FCSTD DOCUMENT  (FreeCAD 0.20R29410 (Git))
Label: StarTrekInsigniaExtrusion
License: All rights reserved
LicenseURL: http://en.wikipedia.org/wiki/All_rights_reserved
objects: Sketcher::SketchObject×2, Image::ImagePlane×1, Part::Part2DObjectPython×1, PartDesign::Body×1
note: 4 computed .brp shape members not serialized (recipe doc carries the construction recipe); baked Part::Feature solids carry a one-line shape summary decoded from their .brp

FEATURE [Image::ImagePlane] ImagePlane
  Placement = pos=(-0.5,-5,0) rot=(0,0,1;0rad)
  XSize = 37.5907
  YSize = 60.1187
FEATURE [Sketcher::SketchObject] Sketch
  FullyConstrained = true
  MapMode = 5
  Support = -> [XY_Plane]
  sketch-geometry (74):
    g0-g3: Circle x4 (B-spline internal-alignment scaffolding for g4; pole/knot coordinates omitted)
    g4: BSplineCurve PolesCount=4 KnotsCount=2 Degree=3 IsPeriodic=0
    g5: GeomPoint X=-18.4513 Y=-34.513 Z=0
    g6: GeomPoint X=-0.733176 Y=25.0097 Z=0
    g7-g10: Circle x4 (B-spline internal-alignment scaffolding for g11; pole/knot coordinates omitted)
    g11: BSplineCurve PolesCount=4 KnotsCount=2 Degree=3 IsPeriodic=0
    g12: GeomPoint X=-0.733176 Y=25.0097 Z=0
    g13: GeomPoint X=17.9425 Y=-29.3614 Z=0
    g14-g22: Circle x9 (B-spline internal-alignment scaffolding for g23; pole/knot coordinates omitted)
    g23: BSplineCurve PolesCount=9 KnotsCount=7 Degree=3 IsPeriodic=0
    g24-g30: GeomPoint x7 (B-spline internal-alignment scaffolding for g23; pole/knot coordinates omitted)
    g31-g34: Circle x4 (B-spline internal-alignment scaffolding for g35; pole/knot coordinates omitted)
    g35: BSplineCurve PolesCount=4 KnotsCount=2 Degree=3 IsPeriodic=0
    g36: GeomPoint X=-16.2191 Y=-26.8064 Z=0
    g37: GeomPoint X=-0.795845 Y=21.9646 Z=0
    g38-g41: Circle x4 (B-spline internal-alignment scaffolding for g42; pole/knot coordinates omitted)
    g42: BSplineCurve PolesCount=4 KnotsCount=2 Degree=3 IsPeriodic=0
    g43: GeomPoint X=-0.795845 Y=21.9646 Z=0
    g44: GeomPoint X=14.3586 Y=-17.0278 Z=0
    g45-g54: Circle x10 (B-spline internal-alignment scaffolding for g55; pole/knot coordinates omitted)
    g55: BSplineCurve PolesCount=10 KnotsCount=8 Degree=3 IsPeriodic=0
    g56-g63: GeomPoint x8 (B-spline internal-alignment scaffolding for g55; pole/knot coordinates omitted)
    g64: LineSegment StartX=0 StartY=17.9558 StartZ=0 EndX=-1.83675 EndY=1.71768 EndZ=0
    g65: LineSegment StartX=-1.83675 StartY=1.71768 StartZ=0 EndX=-5.87472 EndY=0.00675 EndZ=0
    g66: LineSegment StartX=-5.87472 StartY=0.00675 StartZ=0 EndX=-2.54091 EndY=-1.79051 EndZ=0
    g67: LineSegment StartX=-2.54091 StartY=-1.79051 StartZ=0 EndX=-3.15906 EndY=-7.34318 EndZ=0
    g68: LineSegment StartX=-3.15906 StartY=-7.34318 StartZ=0 EndX=4e-16 EndY=-2.82733 EndZ=0
    g69: LineSegment StartX=4e-16 StartY=-2.82733 StartZ=0 EndX=3.15906 EndY=-7.34318 EndZ=0
    g70: LineSegment StartX=3.15906 StartY=-7.34318 StartZ=0 EndX=2.54091 EndY=-1.79051 EndZ=0
    g71: LineSegment StartX=2.54091 StartY=-1.79051 StartZ=0 EndX=5.87472 EndY=0.00675 EndZ=0
    g72: LineSegment StartX=5.87472 StartY=0.00675 StartZ=0 EndX=1.83675 EndY=1.71768 EndZ=0
    g73: LineSegment StartX=1.83675 StartY=1.71768 StartZ=0 EndX=0 EndY=17.9558 EndZ=0
  constraints (74):
    c: Weight(g0) = 1
    c: Equal(g0,g1)
    c: Equal(g0,g2)
    c: Equal(g0,g3)
    c: InternalAlignment(g0-g3 -> g4) x4
    c: InternalAlignment(g5,g4)
    c: InternalAlignment(g6,g4)
    c: Weight(g7) = 1
    c: Coincident(g11,g4)
    c: Equal(g7,g8)
    c: Equal(g7,g9)
    c: Equal(g7,g10)
    c: InternalAlignment(g7-g10 -> g11) x4
    c: InternalAlignment(g12,g11)
    c: InternalAlignment(g13,g11)
    c: Weight(g14) = 1
    c: Coincident(g23,g4)
    c: Equal(g14, g15-g22) x8
    c: Coincident(g23,g11)
    c: InternalAlignment(g14-g22 -> g23) x9
    c: InternalAlignment(g24-g30 -> g23) x7
    c: Weight(g31) = 1
    c: Equal(g31,g32)
    c: Equal(g31,g33)
    c: Equal(g31,g34)
    c: InternalAlignment(g31-g34 -> g35) x4
    c: InternalAlignment(g36,g35)
    c: InternalAlignment(g37,g35)
    c: Weight(g38) = 1
    c: Coincident(g42,g35)
    c: Equal(g38,g39)
    c: Equal(g38,g40)
    c: Equal(g38,g41)
    c: InternalAlignment(g38-g41 -> g42) x4
    c: InternalAlignment(g43,g42)
    c: InternalAlignment(g44,g42)
    c: Weight(g45) = 1
    c: Coincident(g55,g35)
    c: Equal(g45, g46-g54) x9
    c: Coincident(g55,g42)
    c: InternalAlignment(g45-g54 -> g55) x10
    c: InternalAlignment(g56-g63 -> g55) x8
    c: PointOnObject(g64,g-2)
    c: Coincident(g64,g65)
    c: Coincident(g65,g66)
    c: Coincident(g66,g67)
    c: Coincident(g67,g68)
    c: PointOnObject(g68,g-2)
    c: Coincident(g68,g69)
    c: Coincident(g69,g70)
    c: Coincident(g70,g71)
    c: Coincident(g71,g72)
    c: Coincident(g72,g73)
    c: Coincident(g73,g64)
    c: Symmetric(g64,g72,g-2)
    c: Symmetric(g66,g70,g-2)
    c: Symmetric(g67,g69,g-2)
    c: Symmetric(g65,g71,g-2)
    c: Block(g4)
    c: Block(g35)
    c: Block(g55)
    c: Block(g23)
    c: Block(g42)
    c: Block(g11)
    c: Block(g64)
    c: Block(g65)
    c: Block(g66)
    c: Block(g67)
    c: Block(g68)
    c: Block(g69)
    c: Block(g70)
    c: Block(g71)
    c: Block(g72)
    c: Block(g73)
FEATURE [Part::Part2DObjectPython] Clone2D  label="Sketch (2D)"  # Draft 2D object (typed FeaturePython)
  Fuse = false
  Objects = -> [Sketch]
  Scale = (1,1,1)
FEATURE [Sketcher::SketchObject] Sketch001
  ExternalGeometry = -> [Clone2D]
  FullyConstrained = true
  MapMode = 5
  Support = -> [XY_Plane]
FEATURE [PartDesign::Body] Body
  Group = -> [Sketch001,Clone2D]
  Origin = -> Origin
